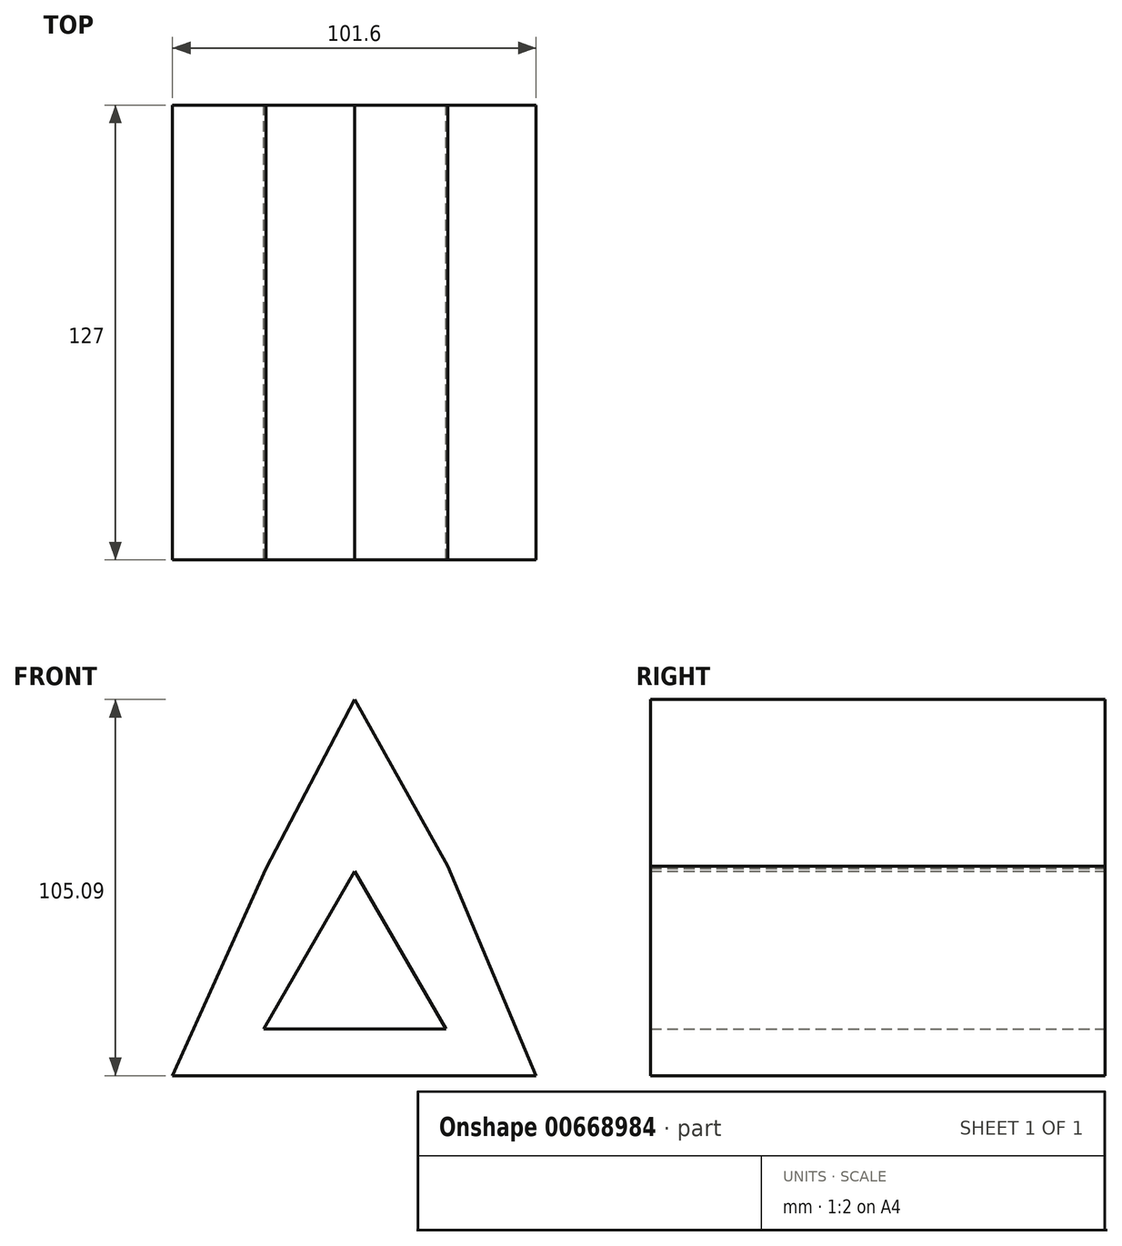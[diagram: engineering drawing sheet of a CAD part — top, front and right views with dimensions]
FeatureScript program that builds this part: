
annotation { "Feature Type Name" : "Feature", "Feature Type Description" : "" }
export const myFeature = defineFeature(function(context is Context, id is Id, definition is map)
    precondition{}
    {
        {
            var Q0;
            Q0=qCreatedBy(makeId("Front.planeOp"),FACE);
            var sketch = newSketch(context, id + "F0", { "sketchPlane" : qUnion([Q0])});
            skLineSegment(sketch, "E0", {"start": v(-50.93, -29.4) * mm, "end": v(50.67, -29.4) * mm});
            skLineSegment(sketch, "E1", {"start": v(50.67, -29.4) * mm, "end": v(25.94, 29.09) * mm});
            skLineSegment(sketch, "E2", {"start": v(-50.93, -29.4) * mm, "end": v(-24.86, 28.5) * mm});
            skLineSegment(sketch, "E3", {"start": v(-24.86, 28.5) * mm, "end": v(0, 75.7) * mm});
            skLineSegment(sketch, "E4", {"start": v(0, 75.7) * mm, "end": v(25.94, 29.09) * mm});
            skLineSegment(sketch, "E5", {"start": v(25.4, -16.33) * mm, "end": v(-25.4, -16.33) * mm});
            skLineSegment(sketch, "E6", {"start": v(-25.4, -16.33) * mm, "end": v(0, 27.67) * mm});
            skLineSegment(sketch, "E7", {"start": v(0, 27.67) * mm, "end": v(25.4, -16.33) * mm});
            skSolve(sketch);
        }
        {
            var Q0;
            Q0 = qSketchRegion(id + "F0", true);
            extrude(context, id + "F1", {"entities" : qUnion([Q0]), "depth" : 127 * mm, "offsetDistance" : 25.4 * mm, "symmetric" : true});
        }
    });
